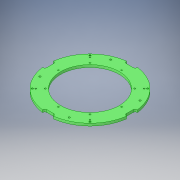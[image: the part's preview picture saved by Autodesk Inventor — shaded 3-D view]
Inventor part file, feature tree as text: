
AUTODESK INVENTOR PART (.ipt)
format: ipt  version: 2016 SP1 (Build 200210100, 210)  size: 203,776 bytes
history: native  units: in
note: dims shown in document units (in); Inventor stores cm internally (conversion verified against a paired STEP export)
features: pattern_circular x4, sketch x4, hole x3, extrude x1, other x1
ambient origin geometry x8: Origin, YZ Plane, XZ Plane, XY Plane, X Axis, Y Axis, Z Axis, Center Point
bodies: Solid1 (feature_tree)
feature tree (13):
  hole  "Hole1"  [1 undecoded]
  pattern_circular  "Circular Pattern2"  Count=4 Angle=360.0deg
  extrude  "Extrusion2"  Depth=1.0in TaperAngle=0.0deg
  pattern_circular  "Circular Pattern6"  Count=4 Angle=360.0deg
  hole  "Hole4"  [1 undecoded]
  pattern_circular  "Circular Pattern7"  Count=4 Angle=360.0deg
  hole  "Hole5"  [1 undecoded]
  pattern_circular  "Circular Pattern8"  [2 undecoded]
  sketch  "Sketch1"  dims[d1=5.875in d2=22.5deg]
  sketch  "Sketch7"  dims[d3=0.266in d4=0.75in d5=0.507in d6=0.25in d7=0.5635in d8=1.0in d9=0.8108in d13=1.5748in d14=360.0deg]
  sketch  "Sketch8"  dims[d44=1.0in d45=1.0in d46=0.0in d47=1.5748in d48=360.0deg]
  sketch  "Sketch9"  dims[d50=0.228in d51=0.75in d52=0.438in d53=0.25in d54=0.5635in d55=1.0in d56=0.8108in d57=1.5748in d58=360.0deg d60=0.211in d61=0.5in d62=0.507in d63=0.25in d64=0.5635in d65=0.679in d66=0.8108in d67=1.5748in d68=360.0deg]
  parser-record x1  (decoder bookkeeping rows leaked as tree rows — omitted from the tree; the rows remain in map.json)
note: 5 required parameter values undecoded (feature->parameter linkage not recoverable at this tier; creation-order binding heuristic only, values carry confidence <= 0.55)
